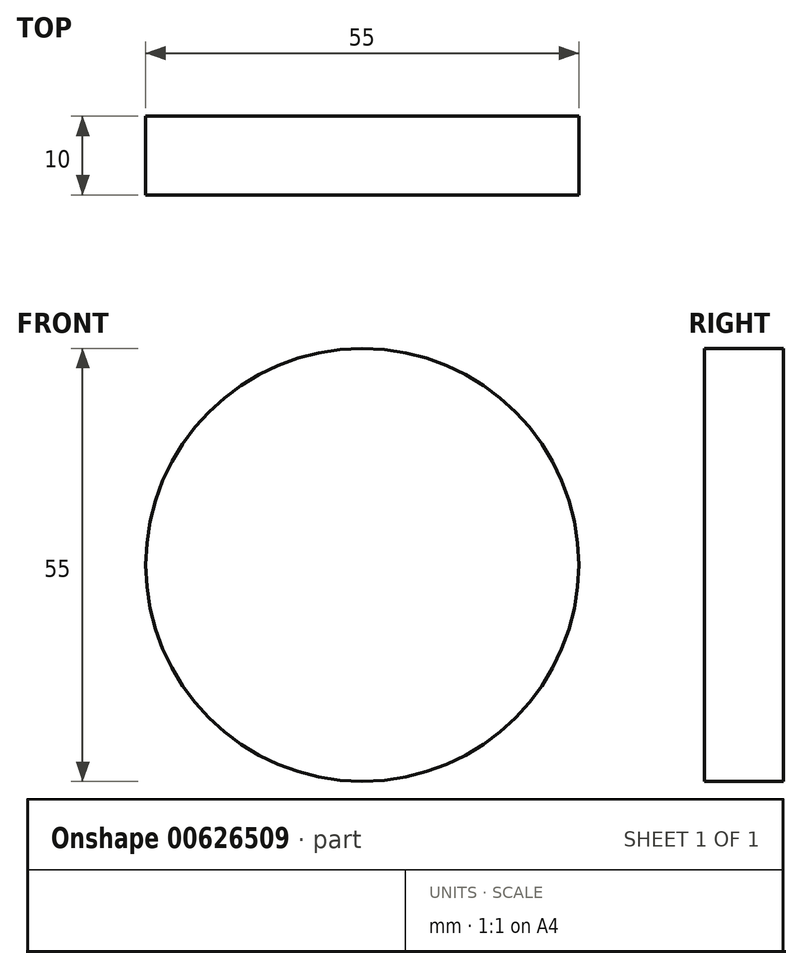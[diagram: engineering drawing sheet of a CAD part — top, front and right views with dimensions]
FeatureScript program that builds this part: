
annotation { "Feature Type Name" : "Feature", "Feature Type Description" : "" }
export const myFeature = defineFeature(function(context is Context, id is Id, definition is map)
    precondition{}
    {
        {
            var Q0;
            Q0=qCreatedBy(makeId("Front.planeOp"),FACE);
            var sketch = newSketch(context, id + "F0", { "sketchPlane" : qUnion([Q0])});
            skCircle(sketch, "E0", {"center": v(0, 0) * mm, "radius": 27.5 * mm});
            skSolve(sketch);
        }
        {
            var Q0;
            Q0=makeQuery(id+"F0.imprint","IMPRINT",FACE,{"disambiguationData":[TD([[makeQuery(id+"F0.imprint","IMPRINT",EDGE,{"derivedFrom":sQuery(id+"F0.wireOp",EDGE,"E0")}),1.0]])]});
            extrude(context, id + "F1", {"entities" : qUnion([Q0]), "depth" : 10 * mm, "offsetDistance" : 25.4 * mm});
        }
    });
